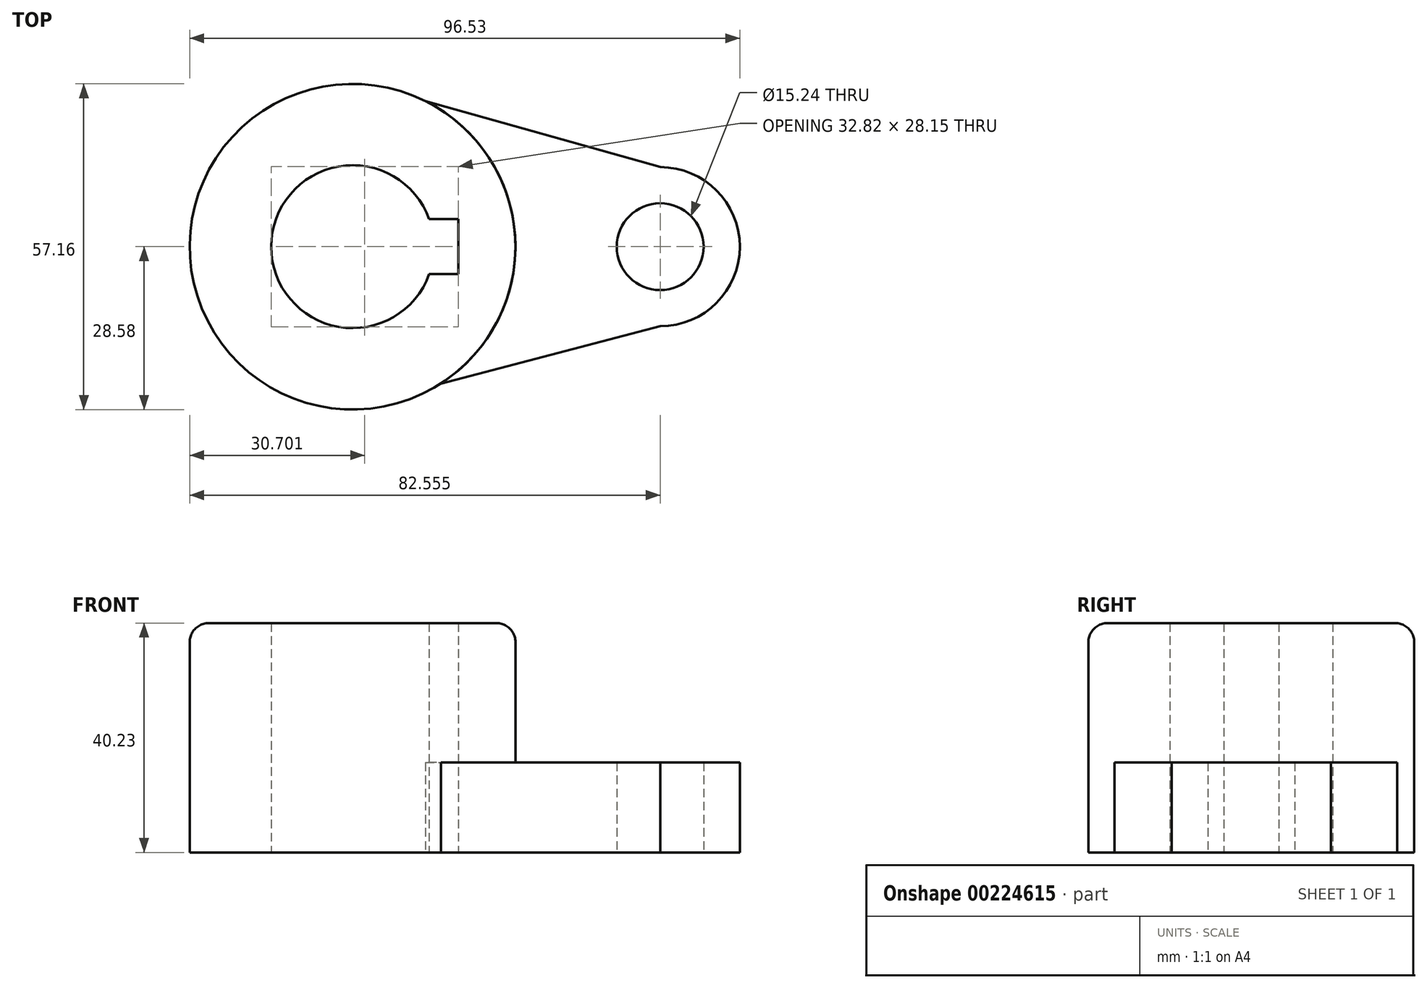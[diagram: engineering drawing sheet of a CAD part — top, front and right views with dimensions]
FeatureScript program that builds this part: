
annotation { "Feature Type Name" : "Feature", "Feature Type Description" : "" }
export const myFeature = defineFeature(function(context is Context, id is Id, definition is map)
    precondition{}
    {
        {
            var Q0;
            Q0=qCreatedBy(makeId("Top.planeOp"),FACE);
            var sketch = newSketch(context, id + "F0", { "sketchPlane" : qUnion([Q0])});
            skLineSegment(sketch, "E0", {"start": v(0, 0) * mm, "end": v(53.98, 0) * mm});
            skCircle(sketch, "E1", {"center": v(0, 0) * mm, "radius": 28.58 * mm});
            skCircle(sketch, "E2", {"center": v(53.98, 0) * mm, "radius": 7.62 * mm});
            skCircle(sketch, "E3", {"center": v(53.98, 0) * mm, "radius": 13.97 * mm});
            skLineSegment(sketch, "E4", {"start": v(53.98, 0) * mm, "end": v(53.98, -13.97) * mm});
            skLineSegment(sketch, "E5", {"start": v(53.98, 0) * mm, "end": v(53.98, 13.97) * mm});
            skLineSegment(sketch, "E6", {"start": v(12.78, 25.56) * mm, "end": v(53.98, 13.97) * mm});
            skLineSegment(sketch, "E7", {"start": v(15.48, -24.02) * mm, "end": v(53.97, -13.97) * mm});
            skCircle(sketch, "E8", {"center": v(0, 0) * mm, "radius": 14.29 * mm});
            skLineSegment(sketch, "E9", {"start": v(0, 0) * mm, "end": v(18.53, 0) * mm});
            skPoint(sketch, "E9.endSnap0", {"position": v(26.99, 0) * mm});
            skLineSegment(sketch, "E10", {"start": v(18.53, 0) * mm, "end": v(18.53, 4.83) * mm});
            skLineSegment(sketch, "E11", {"start": v(18.53, 0) * mm, "end": v(18.53, -4.83) * mm});
            skLineSegment(sketch, "E12", {"start": v(18.53, 4.83) * mm, "end": v(10.9, 4.83) * mm});
            skLineSegment(sketch, "E13", {"start": v(18.53, -4.83) * mm, "end": v(10.9, -4.83) * mm});
            skLineSegment(sketch, "E14", {"start": v(10.9, 4.83) * mm, "end": v(10.9, -4.83) * mm});
            skSolve(sketch);
        }
        {
            var Q0;
            {var subQ9=sQuery(id+"F0.wireOp",EDGE,"E10");Q0=makeQuery(id+"F0.imprint","IMPRINT",FACE,{"disambiguationData":[TD([[makeQuery(id+"F0.imprint","IMPRINT",EDGE,{"derivedFrom":subQ9}),-1.0]])]});}
            extrude(context, id + "F1", {"entities" : qUnion([Q0]), "depth" : 40.23 * mm});
        }
        {
            var Q0;
            {var subQ5=sQuery(id+"F0.wireOp",EDGE,"E6");Q0=makeQuery(id+"F0.imprint","IMPRINT",FACE,{"disambiguationData":[TD([[makeQuery(id+"F0.imprint","IMPRINT",EDGE,{"derivedFrom":subQ5}),-1.0]])]});}
            var Q1;
            {var subQ5=sQuery(id+"F0.wireOp",EDGE,"E7");Q1=makeQuery(id+"F0.imprint","IMPRINT",FACE,{"disambiguationData":[TD([[makeQuery(id+"F0.imprint","IMPRINT",EDGE,{"derivedFrom":subQ5}),1.0]])]});}
            var Q2;
            {var subQ0=sQuery(id+"F0.wireOp",EDGE,"E3");var subQ1=sQuery(id+"F0.wireOp",EDGE,"E0");var subQ2=makeQuery(id+"F0.imprint","INTERSECT",VERTEX,{"derivedFrom":[subQ1,subQ0]});Q2=makeQuery(id+"F0.imprint","IMPRINT",FACE,{"disambiguationData":[TD([[makeQuery(id+"F0.imprint","IMPRINT",EDGE,{"disambiguationData":[TD([[subQ2,-1.0]])],"derivedFrom":subQ1}),-1.0]])]});}
            var Q3;
            {var subQ0=sQuery(id+"F0.wireOp",EDGE,"E3");var subQ1=sQuery(id+"F0.wireOp",EDGE,"E0");var subQ2=makeQuery(id+"F0.imprint","INTERSECT",VERTEX,{"derivedFrom":[subQ1,subQ0]});Q3=makeQuery(id+"F0.imprint","IMPRINT",FACE,{"disambiguationData":[TD([[makeQuery(id+"F0.imprint","IMPRINT",EDGE,{"disambiguationData":[TD([[subQ2,-1.0]])],"derivedFrom":subQ1}),1.0]])]});}
            var Q4;
            {var subQ0=sQuery(id+"F0.wireOp",EDGE,"E5");var subQ1=sQuery(id+"F0.wireOp",EDGE,"E2");var subQ2=makeQuery(id+"F0.imprint","INTERSECT",VERTEX,{"derivedFrom":[subQ1,subQ0]});Q4=makeQuery(id+"F0.imprint","IMPRINT",FACE,{"disambiguationData":[TD([[makeQuery(id+"F0.imprint","IMPRINT",EDGE,{"disambiguationData":[TD([[subQ2,1.0]])],"derivedFrom":subQ1}),-1.0]])]});}
            extrude(context, id + "F2", {"entities" : qUnion([Q0, Q1, Q2, Q3, Q4]), "operationType" : NewBodyOperationType.ADD, "depth" : 15.77 * mm});
        }
        {
            var Q0;
            Q0=makeQuery(id+"F1.opExtrude","CAP_EDGE",EDGE,{"disambiguationData":[OSD([sQuery(id+"F0.wireOp",EDGE,"E1")])],"isStart":false});
            fillet(context, id + "F3", {"entities" : qUnion([Q0]), "radius" : 3.3 * mm, "tangentPropagation" : true, "allowEdgeOverflow" : false});
        }
    });
